# Revit family: xFaucet-Single_Lever-GROHE-Eurosmart-30306_Series
name_source: partatom
category: Plumbing Fixtures
revit_build: Autodesk Revit 2014 (Build: 20130308_1515(x64)
units: mm (PartAtom-declared; Revit-internal decimal feet)

## types (2) — shared parameters
Assembly Code = D2020
CW Connection = Yes
CWFU = 1.5
Cold Water Connection Diameter = 3/8"
Cold Water Connection Radius = 3/16"
Default Elevation = 0"
Description = Eurosmart Single-lever sink mixer 1/2"
HW Connection = Yes
HWFU = 1.5
Height = 7 1/4"
Hot Water Connection Diameter = 0"
Hot Water Connection Radius = 3/16"
Installation Type = Deck Mounted
Length = 8 7/8"
Manufacturer = GROHE
Price = Prices may vary. Please consult Manufacturer Representative for most up-to-date price list.
Product Page URL = http://www.grohe.com
URL = http://www.grohe.com
Vent Connection = No
WFU = 2
Warranty Information = Limited Lifetime Warranty
Waste Connection = No
Width = 2"

## per-type parameters (varying)
| type | Finish | Material |
| 30306000 | Metal-GROHE-000-Starlight Chrome | Metal-GROHE-000-Starlight Chrome |
| 30306DC0 | Metal-GROHE-DC0-Supersteel | Metal-GROHE-DC0-Supersteel |

note: column(s) folded — value = type name in every type: Model

## geometry (parser evidence)
native form markers: Sweep x1
no freeform markers — native parametric forms only
